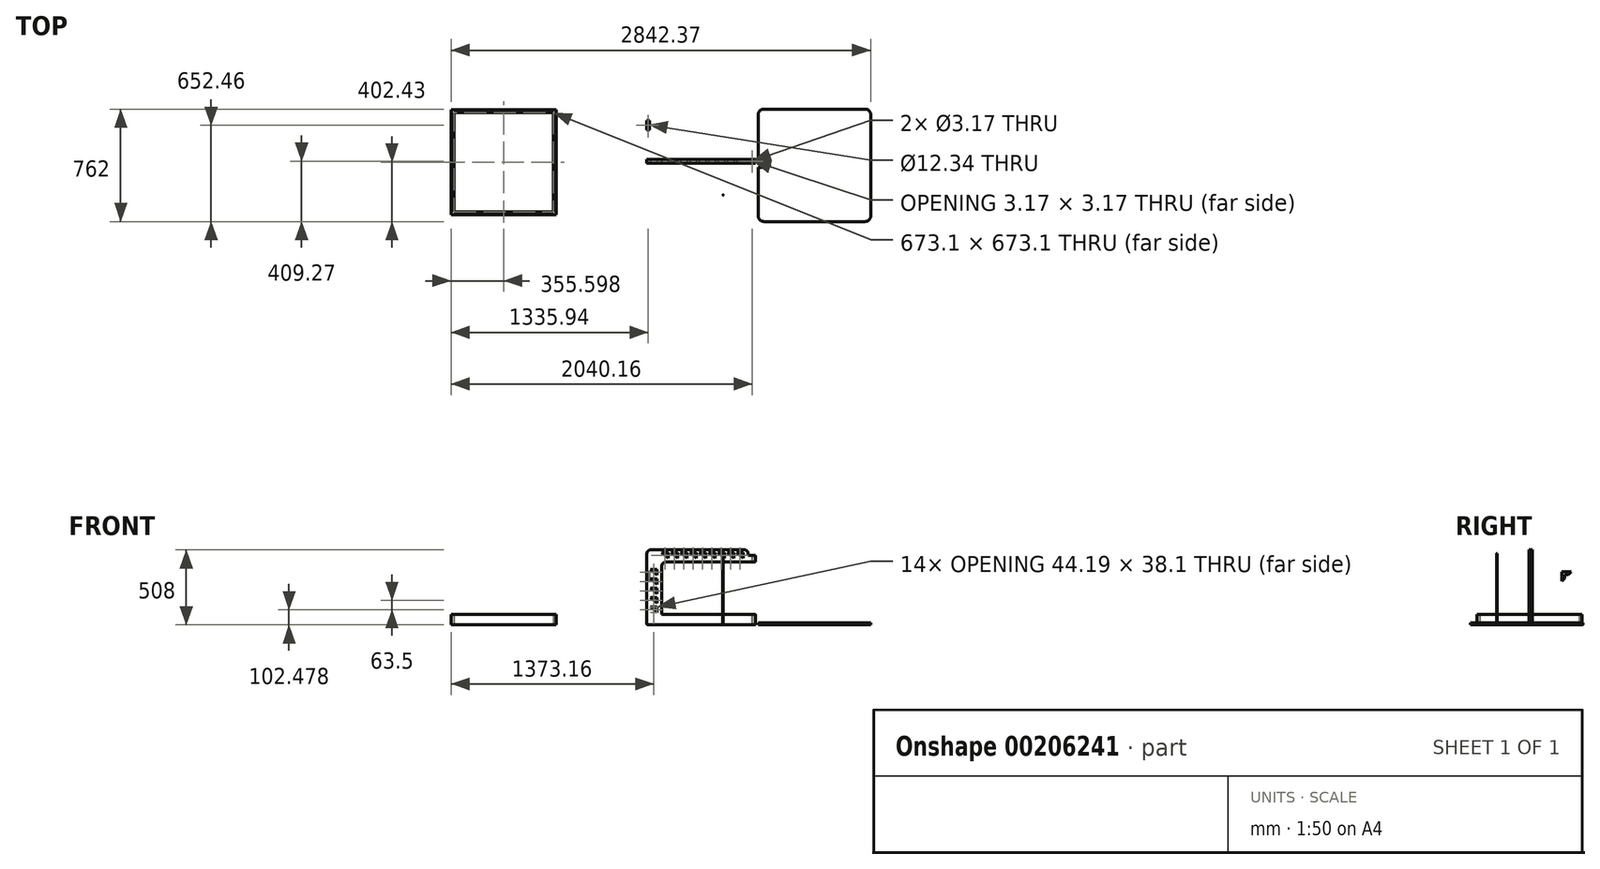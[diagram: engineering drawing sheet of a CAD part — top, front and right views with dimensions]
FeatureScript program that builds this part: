
annotation { "Feature Type Name" : "Feature", "Feature Type Description" : "" }
export const myFeature = defineFeature(function(context is Context, id is Id, definition is map)
    precondition{}
    {
        {
            var Q0;
            Q0=qCreatedBy(makeId("Front.planeOp"),FACE);
            var sketch = newSketch(context, id + "F0", { "sketchPlane" : qUnion([Q0])});
            skLineSegment(sketch, "E0.bottom", {"start": v(0, 0) * mm, "end": v(736.6, 0) * mm});
            skLineSegment(sketch, "E0.top", {"start": v(0, 508) * mm, "end": v(736.6, 508) * mm});
            skLineSegment(sketch, "E0.left", {"start": v(0, 0) * mm, "end": v(0, 508) * mm});
            skLineSegment(sketch, "E0.right", {"start": v(736.6, 0) * mm, "end": v(736.6, 508) * mm});
            skLineSegment(sketch, "E1.bottom", {"start": v(736.6, 69.85) * mm, "end": v(101.6, 69.85) * mm});
            skLineSegment(sketch, "E1.top", {"start": v(736.6, 425.45) * mm, "end": v(101.6, 425.45) * mm});
            skLineSegment(sketch, "E1.left", {"start": v(736.6, 69.85) * mm, "end": v(736.6, 425.45) * mm});
            skLineSegment(sketch, "E1.right", {"start": v(101.6, 69.85) * mm, "end": v(101.6, 425.45) * mm});
            skLineSegment(sketch, "E2.bottom", {"start": v(736.6, 508) * mm, "end": v(685.8, 508) * mm});
            skLineSegment(sketch, "E2.top", {"start": v(736.6, 469.9) * mm, "end": v(685.8, 469.9) * mm});
            skLineSegment(sketch, "E2.left", {"start": v(736.6, 508) * mm, "end": v(736.6, 469.9) * mm});
            skLineSegment(sketch, "E2.right", {"start": v(685.8, 508) * mm, "end": v(685.8, 469.9) * mm});
            skSolve(sketch);
        }
        {
            var Q0;
            {var subQ1=sQuery(id+"F0.wireOp",EDGE,"E0.bottom");Q0=makeQuery(id+"F0.imprint","IMPRINT",FACE,{"disambiguationData":[TD([[makeQuery(id+"F0.imprint","IMPRINT",EDGE,{"derivedFrom":subQ1}),1.0]])]});}
            extrude(context, id + "F1", {"entities" : qUnion([Q0]), "depth" : 25.4 * mm});
        }
        {
            var Q0;
            Q0=makeQuery(id+"F1.opExtrude","SWEPT_EDGE",EDGE,{"disambiguationData":[OSD([sQuery(id+"F0.wireOp",EDGE,"E0.top"),sQuery(id+"F0.wireOp",EDGE,"E2.bottom"),sQuery(id+"F0.wireOp",EDGE,"E2.right")])]});
            fillet(context, id + "F2", {"entities" : qUnion([Q0]), "radius" : 25.4 * mm, "tangentPropagation" : true, "allowEdgeOverflow" : false});
        }
        {
            var Q0;
            Q0=makeQuery(id+"F1.opExtrude","SWEPT_EDGE",EDGE,{"disambiguationData":[OSD([sQuery(id+"F0.wireOp",EDGE,"E2.top"),sQuery(id+"F0.wireOp",EDGE,"E2.right")])]});
            fillet(context, id + "F3", {"entities" : qUnion([Q0]), "radius" : 5.08 * mm, "tangentPropagation" : true, "allowEdgeOverflow" : false});
        }
        {
            var Q0;
            Q0=makeQuery(id+"F1.opExtrude","SWEPT_EDGE",EDGE,{"disambiguationData":[OSD([sQuery(id+"F0.wireOp",EDGE,"E0.top"),sQuery(id+"F0.wireOp",EDGE,"E0.left")])]});
            fillet(context, id + "F4", {"entities" : qUnion([Q0]), "radius" : 25.4 * mm, "tangentPropagation" : true, "allowEdgeOverflow" : false});
        }
        {
            var Q0;
            Q0=makeQuery(id+"F1.opExtrude","SWEPT_EDGE",EDGE,{"disambiguationData":[OSD([sQuery(id+"F0.wireOp",EDGE,"E1.top"),sQuery(id+"F0.wireOp",EDGE,"E1.right")])]});
            fillet(context, id + "F5", {"entities" : qUnion([Q0]), "radius" : 25.4 * mm, "tangentPropagation" : true, "allowEdgeOverflow" : false});
        }
        {
            var Q0;
            Q0=makeQuery(id+"F1.opExtrude","SWEPT_EDGE",EDGE,{"disambiguationData":[OSD([sQuery(id+"F0.wireOp",EDGE,"E0.bottom"),sQuery(id+"F0.wireOp",EDGE,"E0.right")])]});
            var Q1;
            Q1=makeQuery(id+"F1.opExtrude","SWEPT_EDGE",EDGE,{"disambiguationData":[OSD([sQuery(id+"F0.wireOp",EDGE,"E0.right"),sQuery(id+"F0.wireOp",EDGE,"E1.bottom"),sQuery(id+"F0.wireOp",EDGE,"E1.left")])]});
            fillet(context, id + "F6", {"entities" : qUnion([Q0, Q1]), "radius" : 5.08 * mm, "tangentPropagation" : true, "allowEdgeOverflow" : false});
        }
        {
            var Q0;
            Q0=makeQuery(id+"F1.opExtrude","SWEPT_EDGE",EDGE,{"disambiguationData":[OSD([sQuery(id+"F0.wireOp",EDGE,"E0.bottom"),sQuery(id+"F0.wireOp",EDGE,"E0.left")])]});
            fillet(context, id + "F7", {"entities" : qUnion([Q0]), "radius" : 5.08 * mm, "tangentPropagation" : true, "allowEdgeOverflow" : false});
        }
        {
            var Q0;
            Q0=makeQuery(id+"F1.opExtrude","CAP_FACE",FACE,{"disambiguationData":[OSD([sQuery(id+"F0.wireOp",EDGE,"E0.bottom"),sQuery(id+"F0.wireOp",EDGE,"E0.top"),sQuery(id+"F0.wireOp",EDGE,"E0.left"),sQuery(id+"F0.wireOp",EDGE,"E0.right"),sQuery(id+"F0.wireOp",EDGE,"E1.bottom"),sQuery(id+"F0.wireOp",EDGE,"E1.top"),sQuery(id+"F0.wireOp",EDGE,"E1.right"),sQuery(id+"F0.wireOp",EDGE,"E2.top"),sQuery(id+"F0.wireOp",EDGE,"E2.right")])],"isStart":false});
            var sketch = newSketch(context, id + "F8", { "sketchPlane" : qUnion([Q0])});
            skLineSegment(sketch, "E3.bottom", {"start": v(145.64, 489.55) * mm, "end": v(101.45, 489.55) * mm});
            skLineSegment(sketch, "E3.left", {"start": v(145.64, 489.55) * mm, "end": v(145.64, 451.45) * mm});
            skLineSegment(sketch, "E4", {"start": v(145.64, 451.45) * mm, "end": v(101.45, 489.55) * mm});
            skLineSegment(sketch, "E5.1.0.0", {"start": v(209.14, 489.55) * mm, "end": v(209.14, 451.45) * mm});
            skLineSegment(sketch, "E5.1.0.1", {"start": v(209.14, 489.55) * mm, "end": v(164.95, 489.55) * mm});
            skLineSegment(sketch, "E5.1.0.2", {"start": v(209.14, 451.45) * mm, "end": v(164.95, 489.55) * mm});
            skLineSegment(sketch, "E5.2.0.0", {"start": v(272.64, 489.55) * mm, "end": v(272.64, 451.45) * mm});
            skLineSegment(sketch, "E5.2.0.1", {"start": v(272.64, 489.55) * mm, "end": v(228.45, 489.55) * mm});
            skLineSegment(sketch, "E5.2.0.2", {"start": v(272.64, 451.45) * mm, "end": v(228.45, 489.55) * mm});
            skLineSegment(sketch, "E5.3.0.0", {"start": v(336.14, 489.55) * mm, "end": v(336.14, 451.45) * mm});
            skLineSegment(sketch, "E5.3.0.1", {"start": v(336.14, 489.55) * mm, "end": v(291.95, 489.55) * mm});
            skLineSegment(sketch, "E5.3.0.2", {"start": v(336.14, 451.45) * mm, "end": v(291.95, 489.55) * mm});
            skLineSegment(sketch, "E5.4.0.0", {"start": v(399.64, 489.55) * mm, "end": v(399.64, 451.45) * mm});
            skLineSegment(sketch, "E5.4.0.1", {"start": v(399.64, 489.55) * mm, "end": v(355.45, 489.55) * mm});
            skLineSegment(sketch, "E5.4.0.2", {"start": v(399.64, 451.45) * mm, "end": v(355.45, 489.55) * mm});
            skLineSegment(sketch, "E5.5.0.0", {"start": v(463.14, 489.55) * mm, "end": v(463.14, 451.45) * mm});
            skLineSegment(sketch, "E5.5.0.1", {"start": v(463.14, 489.55) * mm, "end": v(418.95, 489.55) * mm});
            skLineSegment(sketch, "E5.5.0.2", {"start": v(463.14, 451.45) * mm, "end": v(418.95, 489.55) * mm});
            skLineSegment(sketch, "E5.6.0.0", {"start": v(526.64, 489.55) * mm, "end": v(526.64, 451.45) * mm});
            skLineSegment(sketch, "E5.6.0.1", {"start": v(526.64, 489.55) * mm, "end": v(482.45, 489.55) * mm});
            skLineSegment(sketch, "E5.6.0.2", {"start": v(526.64, 451.45) * mm, "end": v(482.45, 489.55) * mm});
            skLineSegment(sketch, "E5.7.0.0", {"start": v(590.14, 489.55) * mm, "end": v(590.14, 451.45) * mm});
            skLineSegment(sketch, "E5.7.0.1", {"start": v(590.14, 489.55) * mm, "end": v(545.95, 489.55) * mm});
            skLineSegment(sketch, "E5.7.0.2", {"start": v(590.14, 451.45) * mm, "end": v(545.95, 489.55) * mm});
            skLineSegment(sketch, "E5.8.0.0", {"start": v(653.64, 489.55) * mm, "end": v(653.64, 451.45) * mm});
            skLineSegment(sketch, "E5.8.0.1", {"start": v(653.64, 489.55) * mm, "end": v(609.45, 489.55) * mm});
            skLineSegment(sketch, "E5.8.0.2", {"start": v(653.64, 451.45) * mm, "end": v(609.45, 489.55) * mm});
            skLineSegment(sketch, "E5.direction1", {"start": v(145.64, 451.45) * mm, "end": v(209.14, 451.45) * mm, "construction": true});
            skLineSegment(sketch, "E6.bottom", {"start": v(68.83, 375.53) * mm, "end": v(24.65, 375.53) * mm});
            skLineSegment(sketch, "E6.left", {"start": v(68.83, 375.53) * mm, "end": v(68.83, 337.43) * mm});
            skLineSegment(sketch, "E7", {"start": v(68.83, 337.43) * mm, "end": v(24.65, 375.53) * mm});
            skLineSegment(sketch, "E8.0.1.0", {"start": v(68.83, 273.93) * mm, "end": v(24.65, 312.03) * mm});
            skLineSegment(sketch, "E8.0.1.1", {"start": v(68.83, 312.03) * mm, "end": v(24.65, 312.03) * mm});
            skLineSegment(sketch, "E8.0.1.2", {"start": v(68.83, 312.03) * mm, "end": v(68.83, 273.93) * mm});
            skLineSegment(sketch, "E8.0.2.0", {"start": v(68.83, 210.43) * mm, "end": v(24.65, 248.53) * mm});
            skLineSegment(sketch, "E8.0.2.1", {"start": v(68.83, 248.53) * mm, "end": v(24.65, 248.53) * mm});
            skLineSegment(sketch, "E8.0.2.2", {"start": v(68.83, 248.53) * mm, "end": v(68.83, 210.43) * mm});
            skLineSegment(sketch, "E8.0.3.0", {"start": v(68.83, 146.93) * mm, "end": v(24.65, 185.03) * mm});
            skLineSegment(sketch, "E8.0.3.1", {"start": v(68.83, 185.03) * mm, "end": v(24.65, 185.03) * mm});
            skLineSegment(sketch, "E8.0.3.2", {"start": v(68.83, 185.03) * mm, "end": v(68.83, 146.93) * mm});
            skLineSegment(sketch, "E8.0.4.0", {"start": v(68.83, 83.43) * mm, "end": v(24.65, 121.53) * mm});
            skLineSegment(sketch, "E8.0.4.1", {"start": v(68.83, 121.53) * mm, "end": v(24.65, 121.53) * mm});
            skLineSegment(sketch, "E8.0.4.2", {"start": v(68.83, 121.53) * mm, "end": v(68.83, 83.43) * mm});
            skLineSegment(sketch, "E8.direction1", {"start": v(24.65, 375.53) * mm, "end": v(52.59, 375.53) * mm, "construction": true});
            skLineSegment(sketch, "E8.direction2", {"start": v(24.65, 375.53) * mm, "end": v(24.65, 312.03) * mm, "construction": true});
            skSolve(sketch);
        }
        {
            var Q0;
            Q0=makeQuery(id+"F8.imprint","IMPRINT",FACE,{"disambiguationData":[TD([[makeQuery(id+"F8.imprint","IMPRINT",EDGE,{"derivedFrom":sQuery(id+"F8.wireOp",EDGE,"E3.bottom")}),1.0]])]});
            var Q1;
            Q1=makeQuery(id+"F8.imprint","IMPRINT",FACE,{"disambiguationData":[TD([[makeQuery(id+"F8.imprint","IMPRINT",EDGE,{"derivedFrom":sQuery(id+"F8.wireOp",EDGE,"E5.1.0.0")}),-1.0]])]});
            var Q2;
            Q2=makeQuery(id+"F8.imprint","IMPRINT",FACE,{"disambiguationData":[TD([[makeQuery(id+"F8.imprint","IMPRINT",EDGE,{"derivedFrom":sQuery(id+"F8.wireOp",EDGE,"E5.2.0.0")}),-1.0]])]});
            var Q3;
            Q3=makeQuery(id+"F8.imprint","IMPRINT",FACE,{"disambiguationData":[TD([[makeQuery(id+"F8.imprint","IMPRINT",EDGE,{"derivedFrom":sQuery(id+"F8.wireOp",EDGE,"E5.3.0.0")}),-1.0]])]});
            var Q4;
            Q4=makeQuery(id+"F8.imprint","IMPRINT",FACE,{"disambiguationData":[TD([[makeQuery(id+"F8.imprint","IMPRINT",EDGE,{"derivedFrom":sQuery(id+"F8.wireOp",EDGE,"E5.4.0.0")}),-1.0]])]});
            var Q5;
            Q5=makeQuery(id+"F8.imprint","IMPRINT",FACE,{"disambiguationData":[TD([[makeQuery(id+"F8.imprint","IMPRINT",EDGE,{"derivedFrom":sQuery(id+"F8.wireOp",EDGE,"E5.5.0.0")}),-1.0]])]});
            var Q6;
            Q6=makeQuery(id+"F8.imprint","IMPRINT",FACE,{"disambiguationData":[TD([[makeQuery(id+"F8.imprint","IMPRINT",EDGE,{"derivedFrom":sQuery(id+"F8.wireOp",EDGE,"E5.6.0.0")}),-1.0]])]});
            var Q7;
            Q7=makeQuery(id+"F8.imprint","IMPRINT",FACE,{"disambiguationData":[TD([[makeQuery(id+"F8.imprint","IMPRINT",EDGE,{"derivedFrom":sQuery(id+"F8.wireOp",EDGE,"E5.8.0.0")}),-1.0]])]});
            var Q8;
            Q8=makeQuery(id+"F8.imprint","IMPRINT",FACE,{"disambiguationData":[TD([[makeQuery(id+"F8.imprint","IMPRINT",EDGE,{"derivedFrom":sQuery(id+"F8.wireOp",EDGE,"E5.7.0.0")}),-1.0]])]});
            var Q9;
            Q9=makeQuery(id+"F8.imprint","IMPRINT",FACE,{"disambiguationData":[TD([[makeQuery(id+"F8.imprint","IMPRINT",EDGE,{"derivedFrom":sQuery(id+"F8.wireOp",EDGE,"E6.bottom")}),1.0]])]});
            var Q10;
            Q10=makeQuery(id+"F8.imprint","IMPRINT",FACE,{"disambiguationData":[TD([[makeQuery(id+"F8.imprint","IMPRINT",EDGE,{"derivedFrom":sQuery(id+"F8.wireOp",EDGE,"E8.0.1.0")}),-1.0]])]});
            var Q11;
            Q11=makeQuery(id+"F8.imprint","IMPRINT",FACE,{"disambiguationData":[TD([[makeQuery(id+"F8.imprint","IMPRINT",EDGE,{"derivedFrom":sQuery(id+"F8.wireOp",EDGE,"E8.0.2.0")}),-1.0]])]});
            var Q12;
            Q12=makeQuery(id+"F8.imprint","IMPRINT",FACE,{"disambiguationData":[TD([[makeQuery(id+"F8.imprint","IMPRINT",EDGE,{"derivedFrom":sQuery(id+"F8.wireOp",EDGE,"E8.0.3.0")}),-1.0]])]});
            var Q13;
            Q13=makeQuery(id+"F8.imprint","IMPRINT",FACE,{"disambiguationData":[TD([[makeQuery(id+"F8.imprint","IMPRINT",EDGE,{"derivedFrom":sQuery(id+"F8.wireOp",EDGE,"E8.0.4.0")}),-1.0]])]});
            extrude(context, id + "F9", {"entities" : qUnion([Q0, Q1, Q2, Q3, Q4, Q5, Q6, Q7, Q8, Q9, Q10, Q11, Q12, Q13]), "operationType" : NewBodyOperationType.REMOVE, "endBound" : BoundingType.THROUGH_ALL, "oppositeDirection" : true, "depth" : 25.4 * mm});
        }
        {
            var Q0;
            Q0=qCreatedBy(makeId("Top.planeOp"),FACE);
            var sketch = newSketch(context, id + "F10", { "sketchPlane" : qUnion([Q0])});
            skLineSegment(sketch, "E9.bottom", {"start": v(753.95, -421.97) * mm, "end": v(1515.95, -421.97) * mm});
            skLineSegment(sketch, "E9.top", {"start": v(753.95, 340.03) * mm, "end": v(1515.95, 340.03) * mm});
            skLineSegment(sketch, "E9.left", {"start": v(753.95, -421.97) * mm, "end": v(753.95, 340.03) * mm});
            skLineSegment(sketch, "E9.right", {"start": v(1515.95, -421.97) * mm, "end": v(1515.95, 340.03) * mm});
            skSolve(sketch);
        }
        {
            var Q0;
            Q0 = qSketchRegion(id + "F10", true);
            extrude(context, id + "F11", {"entities" : qUnion([Q0]), "depth" : 12.7 * mm});
        }
        {
            var Q0;
            Q0=qCreatedBy(makeId("Top.planeOp"),FACE);
            var sketch = newSketch(context, id + "F12", { "sketchPlane" : qUnion([Q0])});
            skLineSegment(sketch, "E10.bottom", {"start": v(-1326.42, -375.14) * mm, "end": v(-615.22, -375.14) * mm});
            skLineSegment(sketch, "E10.top", {"start": v(-1326.42, 336.06) * mm, "end": v(-615.22, 336.06) * mm});
            skLineSegment(sketch, "E10.left", {"start": v(-1326.42, -375.14) * mm, "end": v(-1326.42, 336.06) * mm});
            skLineSegment(sketch, "E10.right", {"start": v(-615.22, -375.14) * mm, "end": v(-615.22, 336.06) * mm});
            skLineSegment(sketch, "E11.0", {"start": v(-1307.37, 317.01) * mm, "end": v(-634.27, 317.01) * mm});
            skLineSegment(sketch, "E11.1", {"start": v(-1307.37, -356.09) * mm, "end": v(-1307.37, 317.01) * mm});
            skLineSegment(sketch, "E11.2", {"start": v(-1307.37, -356.09) * mm, "end": v(-634.27, -356.09) * mm});
            skLineSegment(sketch, "E11.3", {"start": v(-634.27, -356.09) * mm, "end": v(-634.27, 317.01) * mm});
            skSolve(sketch);
        }
        {
            var Q0;
            Q0=makeQuery(id+"F12.imprint","IMPRINT",FACE,{"disambiguationData":[TD([[makeQuery(id+"F12.imprint","IMPRINT",EDGE,{"derivedFrom":sQuery(id+"F12.wireOp",EDGE,"E10.bottom")}),1.0]])]});
            extrude(context, id + "F13", {"entities" : qUnion([Q0]), "depth" : 69.85 * mm});
        }
        {
            var Q0;
            Q0=makeQuery(id+"F11.opExtrude","CAP_FACE",FACE,{"disambiguationData":[OSD([sQuery(id+"F10.wireOp",EDGE,"E9.bottom"),sQuery(id+"F10.wireOp",EDGE,"E9.top"),sQuery(id+"F10.wireOp",EDGE,"E9.left"),sQuery(id+"F10.wireOp",EDGE,"E9.right")])],"isStart":false});
            var sketch = newSketch(context, id + "F14", { "sketchPlane" : qUnion([Q0])});
            skLineSegment(sketch, "E12.bottom", {"start": v(753.95, -53.67) * mm, "end": v(830.15, -53.67) * mm});
            skLineSegment(sketch, "E12.top", {"start": v(753.95, -28.27) * mm, "end": v(830.15, -28.27) * mm});
            skLineSegment(sketch, "E12.left", {"start": v(753.95, -53.67) * mm, "end": v(753.95, -28.27) * mm});
            skLineSegment(sketch, "E12.right", {"start": v(830.15, -53.67) * mm, "end": v(830.15, -28.27) * mm});
            skSolve(sketch);
        }
        {
            var Q0;
            Q0 = qSketchRegion(id + "F14", true);
            extrude(context, id + "F15", {"entities" : qUnion([Q0]), "operationType" : NewBodyOperationType.REMOVE, "oppositeDirection" : true, "depth" : 25.4 * mm});
        }
        {
            var Q0;
            Q0=makeQuery(id+"F1.opExtrude","SWEPT_FACE",FACE,{"disambiguationData":[OSD([sQuery(id+"F0.wireOp",EDGE,"E2.top")])]});
            var sketch = newSketch(context, id + "F16", { "sketchPlane" : qUnion([Q0])});
            skLineSegment(sketch, "E13", {"start": v(713.74, 0) * mm, "end": v(713.74, -25.4) * mm, "construction": true});
            skLineSegment(sketch, "E14", {"start": v(736.6, -12.7) * mm, "end": v(713.74, -12.7) * mm, "construction": true});
            skCircle(sketch, "E15", {"center": v(713.74, -12.7) * mm, "radius": 1.59 * mm});
            skSolve(sketch);
        }
        {
            var Q0;
            Q0 = qSketchRegion(id + "F16", true);
            extrude(context, id + "F17", {"entities" : qUnion([Q0]), "operationType" : NewBodyOperationType.REMOVE, "endBound" : BoundingType.THROUGH_ALL, "oppositeDirection" : true, "depth" : 25.4 * mm});
        }
        {
            var Q0;
            Q0=qCreatedBy(makeId("Top.planeOp"),FACE);
            var sketch = newSketch(context, id + "F18", { "sketchPlane" : qUnion([Q0])});
            skCircle(sketch, "E16", {"center": v(516.1, -242.1) * mm, "radius": 1.59 * mm});
            skSolve(sketch);
        }
        {
            var Q0;
            Q0 = qSketchRegion(id + "F18", true);
            extrude(context, id + "F19", {"entities" : qUnion([Q0]), "depth" : 482.6 * mm});
        }
        {
            var Q0;
            Q0=makeQuery(id+"F11.opExtrude","SWEPT_EDGE",EDGE,{"disambiguationData":[OSD([sQuery(id+"F10.wireOp",EDGE,"E9.bottom"),sQuery(id+"F10.wireOp",EDGE,"E9.right")])]});
            var Q1;
            Q1=makeQuery(id+"F11.opExtrude","SWEPT_EDGE",EDGE,{"disambiguationData":[OSD([sQuery(id+"F10.wireOp",EDGE,"E9.bottom"),sQuery(id+"F10.wireOp",EDGE,"E9.left")])]});
            var Q2;
            Q2=makeQuery(id+"F11.opExtrude","SWEPT_EDGE",EDGE,{"disambiguationData":[OSD([sQuery(id+"F10.wireOp",EDGE,"E9.top"),sQuery(id+"F10.wireOp",EDGE,"E9.right")])]});
            var Q3;
            Q3=makeQuery(id+"F11.opExtrude","SWEPT_EDGE",EDGE,{"disambiguationData":[OSD([sQuery(id+"F10.wireOp",EDGE,"E9.top"),sQuery(id+"F10.wireOp",EDGE,"E9.left")])]});
            fillet(context, id + "F20", {"entities" : qUnion([Q0, Q1, Q2, Q3]), "radius" : 38.1 * mm, "tangentPropagation" : true, "allowEdgeOverflow" : false});
        }
        {
            var Q0;
            Q0=qCreatedBy(makeId("Right.planeOp"),FACE);
            var sketch = newSketch(context, id + "F21", { "sketchPlane" : qUnion([Q0])});
            skLineSegment(sketch, "E17.top", {"start": v(263.08, 361.26) * mm, "end": v(199.58, 361.26) * mm});
            skLineSegment(sketch, "E17.right", {"start": v(199.58, 297.76) * mm, "end": v(199.58, 361.26) * mm});
            skLineSegment(sketch, "E18", {"start": v(263.08, 361.26) * mm, "end": v(243.2, 341.37) * mm});
            skLineSegment(sketch, "E19", {"start": v(243.2, 341.37) * mm, "end": v(217.8, 341.37) * mm});
            skLineSegment(sketch, "E20", {"start": v(217.8, 341.37) * mm, "end": v(217.8, 315.97) * mm});
            skLineSegment(sketch, "E21.trimOffspring", {"start": v(217.8, 315.97) * mm, "end": v(199.58, 297.76) * mm});
            skSolve(sketch);
        }
        {
            var Q0;
            Q0 = qSketchRegion(id + "F21", true);
            extrude(context, id + "F22", {"entities" : qUnion([Q0]), "depth" : 19.05 * mm});
        }
        {
            var Q0;
            Q0=makeQuery(id+"F22.opExtrude","SWEPT_FACE",FACE,{"disambiguationData":[OSD([sQuery(id+"F21.wireOp",EDGE,"E19")])]});
            var sketch = newSketch(context, id + "F23", { "sketchPlane" : qUnion([Q0])});
            skLineSegment(sketch, "E22", {"start": v(9.53, -243.2) * mm, "end": v(9.53, -217.8) * mm, "construction": true});
            skCircle(sketch, "E23", {"center": v(9.53, -230.5) * mm, "radius": 6.17 * mm});
            skSolve(sketch);
        }
        {
            var Q0;
            Q0 = qSketchRegion(id + "F23", true);
            extrude(context, id + "F24", {"entities" : qUnion([Q0]), "operationType" : NewBodyOperationType.REMOVE, "oppositeDirection" : true, "depth" : 25.4 * mm});
        }
    });
